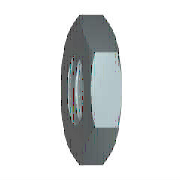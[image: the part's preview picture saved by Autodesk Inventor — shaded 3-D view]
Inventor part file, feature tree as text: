
AUTODESK INVENTOR PART (.ipt)
format: ipt  version: 2022 (Build 260153000, 153)  size: 174,592 bytes
history: native  units: mm (DEFAULTED — no unit token found)
features: sketch x3, other x2, extrude x1, hole x1, plane x1
ambient origin geometry x7: Origin, YZ Plane, XZ Plane, X Axis, Y Axis, Z Axis, Center Point
bodies: Solid1 (feature_tree)
feature tree (8):
  extrude  "Базовый элемент"  Depth=5.773503mm
  other  "Фаска1"
  hole  "Резьба"  [1 undecoded]
  other  "Work Axis1"
  plane  "Work Plane1"
  sketch  "Эскиз1"
  sketch  "Эскиз2"
  sketch  "Эскиз3"
note: 1 required parameter value undecoded (feature->parameter linkage not recoverable at this tier; creation-order binding heuristic only, values carry confidence <= 0.55)
